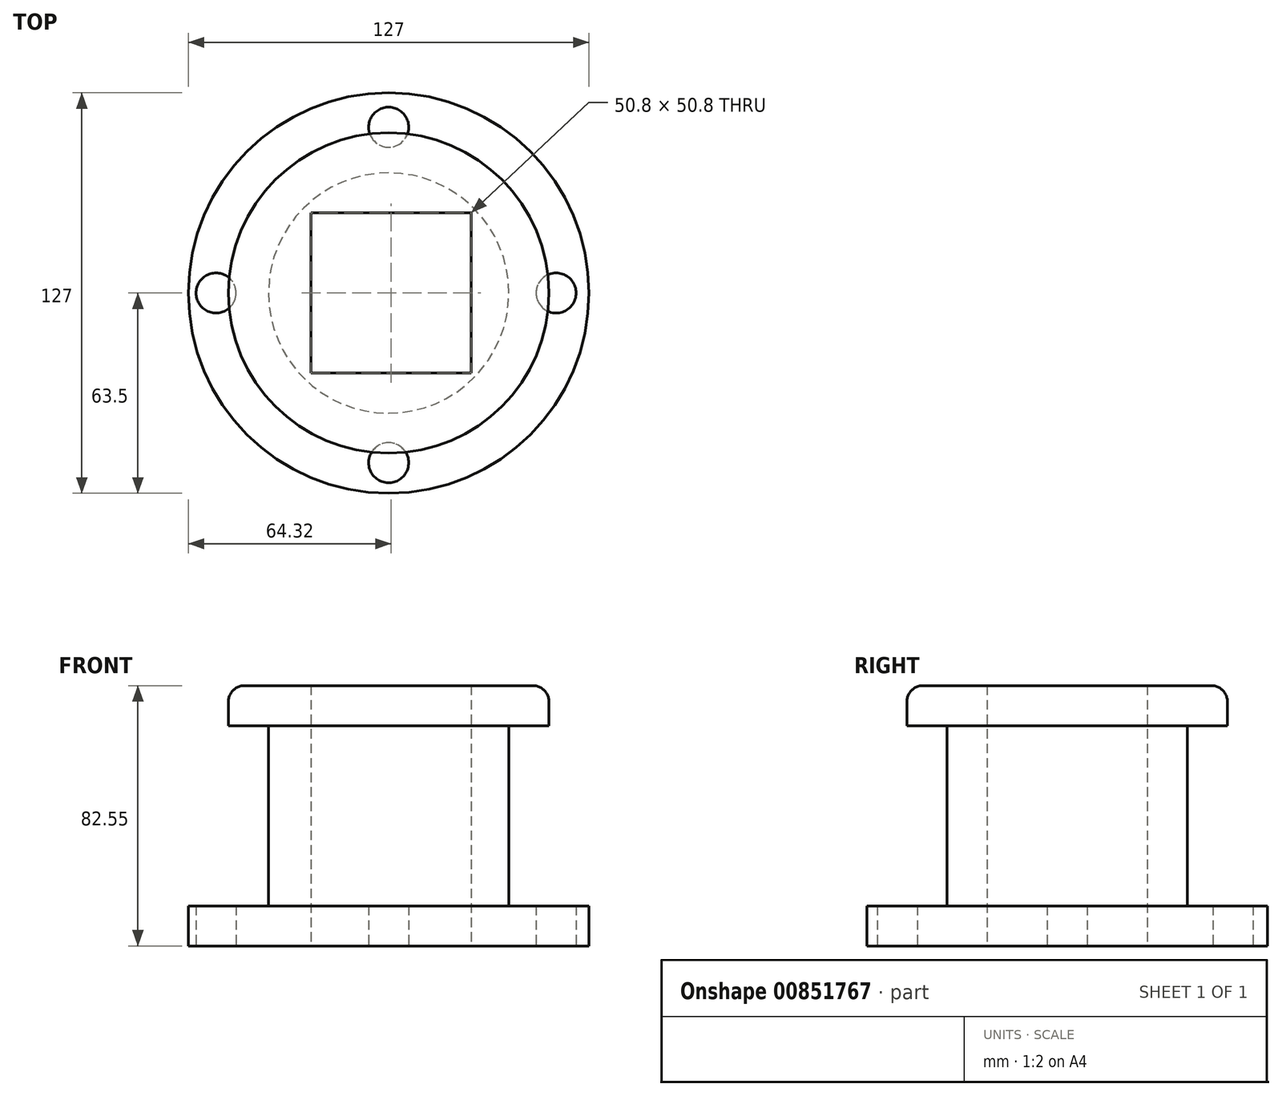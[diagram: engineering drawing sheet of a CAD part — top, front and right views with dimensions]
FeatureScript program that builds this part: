
annotation { "Feature Type Name" : "Feature", "Feature Type Description" : "" }
export const myFeature = defineFeature(function(context is Context, id is Id, definition is map)
    precondition{}
    {
        {
            var Q0;
            Q0=qCreatedBy(makeId("Top.planeOp"),FACE);
            var sketch = newSketch(context, id + "F0", { "sketchPlane" : qUnion([Q0])});
            skLineSegment(sketch, "E0.bottom", {"start": v(-24.58, 25.4) * mm, "end": v(26.22, 25.4) * mm});
            skLineSegment(sketch, "E0.top", {"start": v(-24.58, -25.4) * mm, "end": v(26.22, -25.4) * mm});
            skLineSegment(sketch, "E0.left", {"start": v(-24.58, 25.4) * mm, "end": v(-24.58, -25.4) * mm});
            skLineSegment(sketch, "E0.right", {"start": v(26.22, 25.4) * mm, "end": v(26.22, -25.4) * mm});
            skCircle(sketch, "E1", {"center": v(0, 0) * mm, "radius": 50.8 * mm});
            skSolve(sketch);
        }
        {
            var Q0;
            Q0=makeQuery(id+"F0.imprint","IMPRINT",FACE,{"disambiguationData":[TD([[makeQuery(id+"F0.imprint","IMPRINT",EDGE,{"derivedFrom":sQuery(id+"F0.wireOp",EDGE,"E0.bottom")}),1.0]])]});
            extrude(context, id + "F1", {"entities" : qUnion([Q0]), "depth" : 12.7 * mm, "offsetDistance" : 25.4 * mm});
        }
        {
            var Q0;
            Q0=makeQuery(id+"F1.opExtrude","CAP_EDGE",EDGE,{"disambiguationData":[OSD([sQuery(id+"F0.wireOp",EDGE,"E1")])],"isStart":false});
            fillet(context, id + "F2", {"entities" : qUnion([Q0]), "radius" : 5.08 * mm, "tangentPropagation" : true, "allowEdgeOverflow" : false});
        }
        {
            var Q0;
            Q0=makeQuery(id+"F1.opExtrude","CAP_FACE",FACE,{"disambiguationData":[OSD([sQuery(id+"F0.wireOp",EDGE,"E0.bottom"),sQuery(id+"F0.wireOp",EDGE,"E0.top"),sQuery(id+"F0.wireOp",EDGE,"E0.left"),sQuery(id+"F0.wireOp",EDGE,"E0.right"),sQuery(id+"F0.wireOp",EDGE,"E1")])],"isStart":true});
            var sketch = newSketch(context, id + "F3", { "sketchPlane" : qUnion([Q0])});
            skCircle(sketch, "E2", {"center": v(0, 0) * mm, "radius": 38.1 * mm});
            skSolve(sketch);
        }
        {
            var Q0;
            Q0=qSketchRegion(id+"F3",true);
            extrude(context, id + "F4", {"entities" : qUnion([Q0]), "operationType" : NewBodyOperationType.ADD, "depth" : 57.15 * mm, "offsetDistance" : 25.4 * mm});
        }
        {
            var Q0;
            Q0=makeQuery(id+"F4.opExtrude","CAP_FACE",FACE,{"disambiguationData":[OSD([sQuery(id+"F3.wireOp",EDGE,"E2")])],"isStart":false});
            var sketch = newSketch(context, id + "F5", { "sketchPlane" : qUnion([Q0])});
            skCircle(sketch, "E3", {"center": v(0, 0) * mm, "radius": 63.5 * mm});
            skSolve(sketch);
        }
        {
            var Q0;
            Q0=qSketchRegion(id+"F5",true);
            var Q1;
            Q1=makeQuery(id+"F4.opExtrude","CAP_FACE",FACE,{"disambiguationData":[OSD([sQuery(id+"F3.wireOp",EDGE,"E2")])],"isStart":true});
            extrude(context, id + "F6", {"entities" : qUnion([Q0, Q1]), "operationType" : NewBodyOperationType.ADD, "depth" : 12.7 * mm, "offsetDistance" : 25.4 * mm});
        }
        {
            var Q0;
            Q0=makeQuery(id+"F4.opExtrude","CAP_FACE",FACE,{"disambiguationData":[OSD([sQuery(id+"F3.wireOp",EDGE,"E2")])],"isStart":true});
            extrude(context, id + "F7", {"entities" : qUnion([Q0]), "operationType" : NewBodyOperationType.REMOVE, "oppositeDirection" : true, "depth" : 106.68 * mm, "offsetDistance" : 25.4 * mm});
        }
        {
            var Q0;
            Q0=makeQuery(id+"F6.opExtrude","CAP_FACE",FACE,{"disambiguationData":[OSD([sQuery(id+"F5.wireOp",EDGE,"E3")])],"isStart":false});
            var sketch = newSketch(context, id + "F8", { "sketchPlane" : qUnion([Q0])});
            skCircle(sketch, "E4", {"center": v(-54.72, 0) * mm, "radius": 6.35 * mm});
            skCircle(sketch, "E5", {"center": v(0, 53.81) * mm, "radius": 6.35 * mm});
            skCircle(sketch, "E6", {"center": v(53.1, 0) * mm, "radius": 6.35 * mm});
            skCircle(sketch, "E7", {"center": v(0, -52.6) * mm, "radius": 6.35 * mm});
            skSolve(sketch);
        }
        {
            var Q0;
            Q0=makeQuery(id+"F8.imprint","IMPRINT",FACE,{"disambiguationData":[TD([[makeQuery(id+"F8.imprint","IMPRINT",EDGE,{"derivedFrom":sQuery(id+"F8.wireOp",EDGE,"E7")}),1.0]])]});
            var Q1;
            Q1=makeQuery(id+"F8.imprint","IMPRINT",FACE,{"disambiguationData":[TD([[makeQuery(id+"F8.imprint","IMPRINT",EDGE,{"derivedFrom":sQuery(id+"F8.wireOp",EDGE,"E6")}),1.0]])]});
            var Q2;
            Q2=makeQuery(id+"F8.imprint","IMPRINT",FACE,{"disambiguationData":[TD([[makeQuery(id+"F8.imprint","IMPRINT",EDGE,{"derivedFrom":sQuery(id+"F8.wireOp",EDGE,"E5")}),1.0]])]});
            var Q3;
            Q3=makeQuery(id+"F8.imprint","IMPRINT",FACE,{"disambiguationData":[TD([[makeQuery(id+"F8.imprint","IMPRINT",EDGE,{"derivedFrom":sQuery(id+"F8.wireOp",EDGE,"E4")}),1.0]])]});
            extrude(context, id + "F9", {"entities" : qUnion([Q0, Q1, Q2, Q3]), "operationType" : NewBodyOperationType.REMOVE, "oppositeDirection" : true, "depth" : 12.7 * mm, "offsetDistance" : 25.4 * mm});
        }
    });
